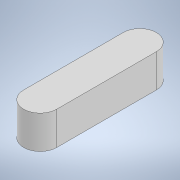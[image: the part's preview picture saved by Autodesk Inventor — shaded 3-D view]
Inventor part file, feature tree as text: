
AUTODESK INVENTOR PART (.ipt)
format: ipt  version: 2022 (Build 260153000, 153)  size: 99,328 bytes
history: native  units: mm
features: extrude x1, fillet x1, sketch x1
ambient origin geometry x8: Origin, YZ Plane, XZ Plane, XY Plane, X Axis, Y Axis, Z Axis, Center Point
bodies: Solid1 (feature_tree)
feature tree (3):
  extrude  "Extrusion1"  Depth=5.0mm
  fillet  "Fillet1"  Radius=20.0mm
  sketch  "Sketch1"  dims[d0=5.0mm d1=5.0mm d2=20.0mm d3=0.0mm d4=2.5mm]
